# Revit family: Camera-Security-Panasonic-Dome-Network-SFN130X
name_source: partatom
category: Security Devices
revit_build: Autodesk Revit 2013 (Build: 20130531_2115(x64)
units: mm (PartAtom-declared; Revit-internal decimal feet)

## types (2) — shared parameters
Audio In = No
Audio Out = No
Communication Ports = 10Base-T / 100Base-TX, RJ-45
Date Last Modified = 2017/01/30
Day Or Night = Yes
Diameter = 4.094 "
Dome Part Number = WV-CW6SA
Equipment Abbreviation = SC
Family Version = 1.0.0
Has POE = Yes
Height = 1.85 "
IP Or Analog = IP
Indoor Or Outdoor = Indoor
Manufacturer = Panasonic
Minimum Illumination = 0 lx
Model Disclaimer = Contact Panasonic for more information
Mounting Positions = Surface Mount
Operational Humidity = 90% or less (without condensation)
Operational Temperature = 32°F - 104°F
Panning Range = -20 to +20
PoE = 48 V
Power Active = 4.3 W
Product Documentation Link = http://ssbu-t.psn-web.net
Product Material = ABS Resin - Panasonic - Sail White
Product Page URL = http://security.panasonic.com
Provide Feedback = https://www.surveymonkey.com
Rated Current = 90 mA
Regulatory Compliance = UL (UL60950-1), C-UL (CAN/CSA C22.2 No.60950-1), CE, IEC60950-1, FCC Part15 ClassA, ICES003 ClassA, EN55022 ClassB, EN55024
Storage Temperature = 32°F - 104°F
Tilting Range = -20 to +90
URL = http://security.panasonic.com
Vandal Resistant = No
Weight = 0.57 lb
Wide Dynamic Range = Yes
z Base Radius = 2.047 "
z Const Pan Handle Length = 27.559 "
z Const Tilt Base Length = 9.843 "
z Const Tilt Base2 Length = 19.685 "
z Const Tilt Handle Length = 9.843 "
z Const Yaw Base Length = 10.236 "
z Const Yaw Base2 Length = 17.323 "
z Const Yaw Handle Length = 9.252 "
z Dome Material = Acrylic Resin - Panasonic - Clear
z VV Viewpoint Depth Max = 0.797 "
z VV Viewpoint Depth Min = 0.797 "
zero-valued in all types: Default Elevation

## per-type parameters (varying)
| type | Angle Of View | Description | HFOV Max 169 | HFOV Max 43 | HFOV Min 169 | HFOV Min 43 | Model | Part Description | Part Number | VFOV Max 169 | VFOV Max 43 | VFOV Min 169 | VFOV Min 43 | z Camera Resolution Type |
| Super Dynamic FullHD, Dome, Network, WV-SFN130 | 108 | Security Camera, Super Dynamic, Full HD, Dome, Network | 108.00° | 89.00° | 108.00° | 89.00° | WV-SFN130 | Security Camera, Super Dynamic, Full HD, Dome, Network | WV-SFN130 | 60.00° | 66.00° | 60.00° | 66.00° | 1 |
| Super Dynamic HD, Dome, Network, WV-SFN110 | 100 | Security Camera, Super Dynamic, HD, Dome, Network | 100.00° | 100.00° | 100.00° | 100.00° | WV-SFN110 | Security Camera, Super Dynamic, HD, Dome, Network | WV-SFN110 | 55.00° | 73.00° | 55.00° | 73.00° | 2 |

## geometry (parser evidence)
native form markers: Sweep x3
no freeform markers — native parametric forms only
